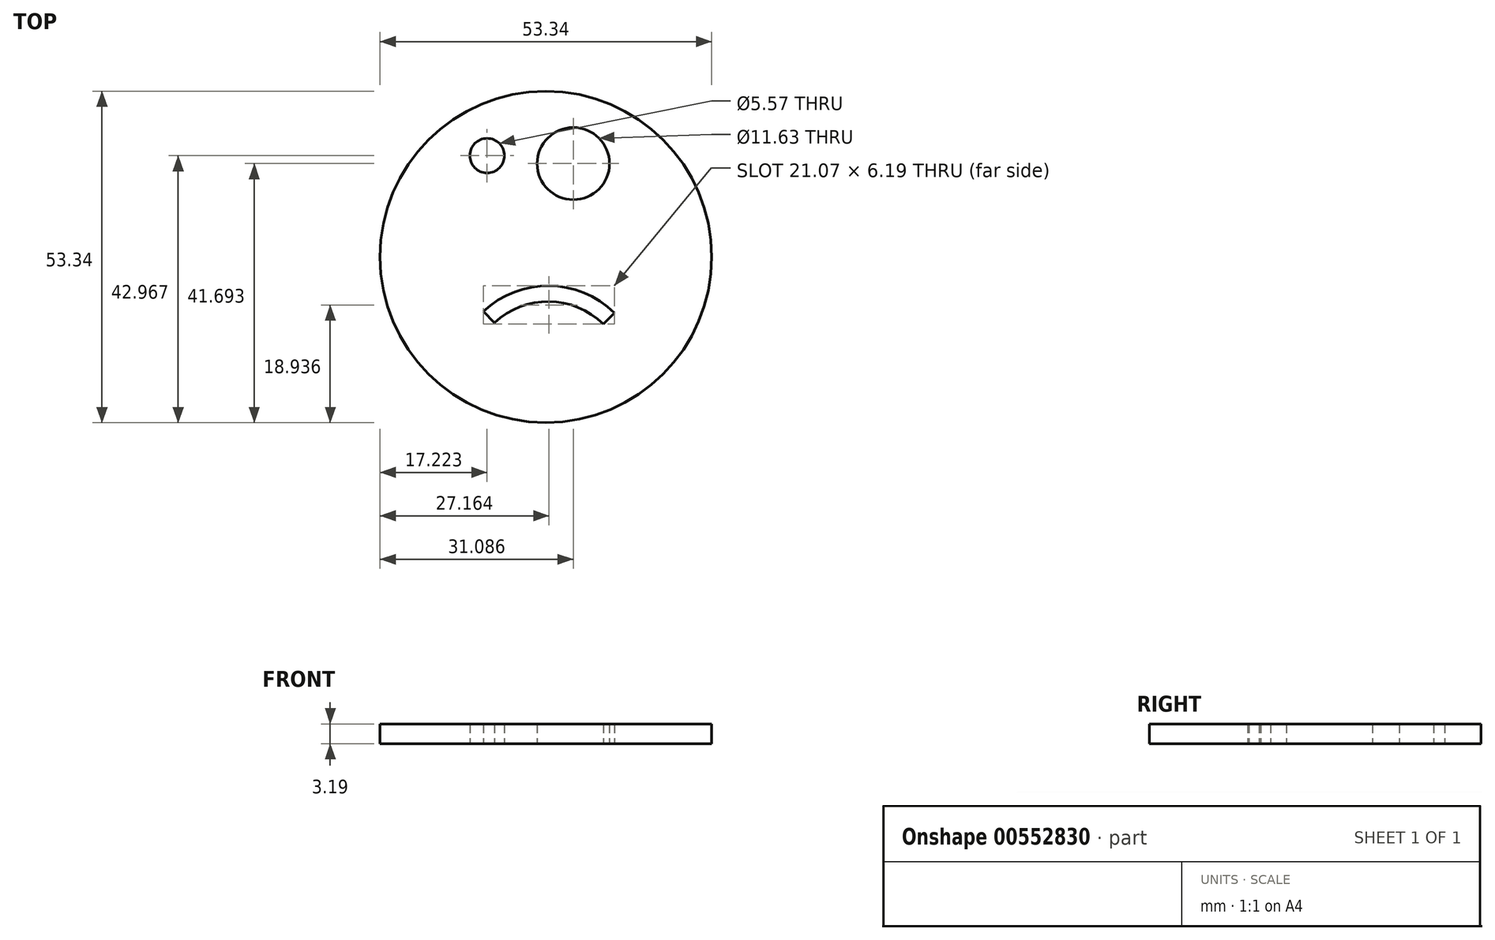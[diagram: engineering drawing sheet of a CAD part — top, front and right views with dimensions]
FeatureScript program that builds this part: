
annotation { "Feature Type Name" : "Feature", "Feature Type Description" : "" }
export const myFeature = defineFeature(function(context is Context, id is Id, definition is map)
    precondition{}
    {
        {
            var Q0;
            Q0=qCreatedBy(makeId("Top.planeOp"),FACE);
            var sketch = newSketch(context, id + "F0", { "sketchPlane" : qUnion([Q0])});
            skCircle(sketch, "E0", {"center": v(-45.56, 22.62) * mm, "radius": 26.67 * mm});
            skArc(sketch, "E1", {"start": v(-34.53, 13.6) * mm, "mid": v(-45.02, 17.98) * mm, "end": v(-55.6, 13.83) * mm});
            skCircle(sketch, "E2", {"center": v(-55, 38.92) * mm, "radius": 2.79 * mm});
            skCircle(sketch, "E3", {"center": v(-41.14, 37.64) * mm, "radius": 5.82 * mm});
            skCircle(sketch, "E4", {"center": v(-41.14, 37.64) * mm, "radius": 1.31 * mm});
            skArc(sketch, "E5.0", {"start": v(-36.32, 11.79) * mm, "mid": v(-45.05, 15.44) * mm, "end": v(-53.85, 11.99) * mm});
            skLineSegment(sketch, "E6", {"start": v(-55.6, 13.83) * mm, "end": v(-53.85, 11.99) * mm});
            skLineSegment(sketch, "E7", {"start": v(-34.53, 13.6) * mm, "end": v(-36.32, 11.79) * mm});
            skSolve(sketch);
        }
        {
            var Q0;
            Q0=makeQuery(id+"F0.imprint","IMPRINT",FACE,{"disambiguationData":[TD([[makeQuery(id+"F0.imprint","IMPRINT",EDGE,{"derivedFrom":sQuery(id+"F0.wireOp",EDGE,"E0")}),1.0]])]});
            extrude(context, id + "F1", {"entities" : qUnion([Q0]), "depth" : 3.19 * mm, "offsetDistance" : 25.4 * mm});
        }
    });
